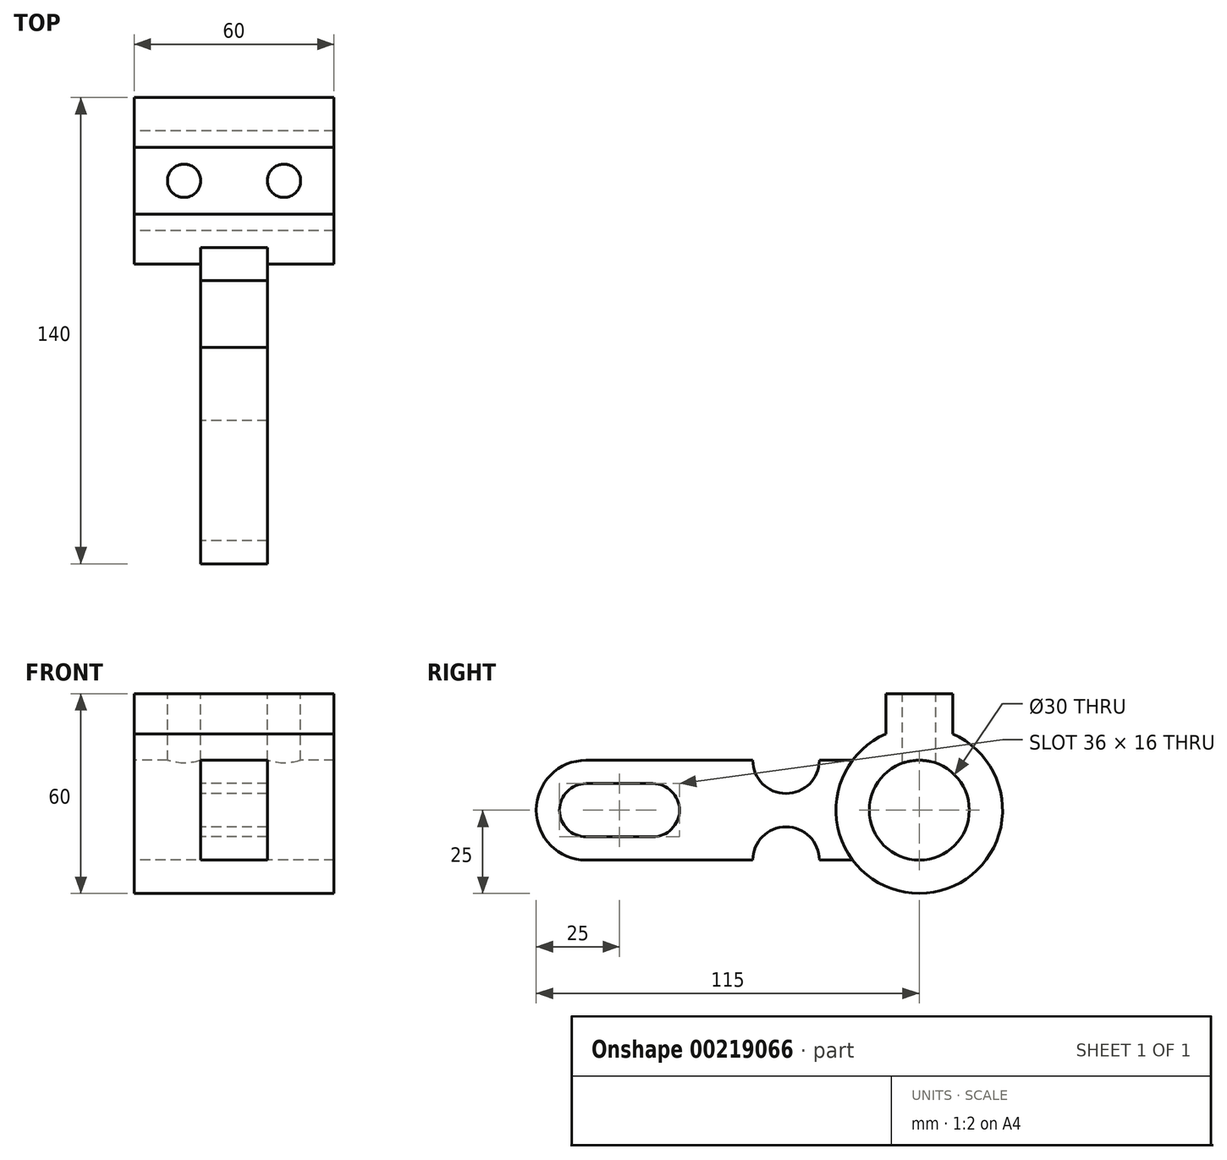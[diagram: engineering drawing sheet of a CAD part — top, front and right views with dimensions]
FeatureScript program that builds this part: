
annotation { "Feature Type Name" : "Feature", "Feature Type Description" : "" }
export const myFeature = defineFeature(function(context is Context, id is Id, definition is map)
    precondition{}
    {
        {
            var Q0;
            Q0=qCreatedBy(makeId("Right.planeOp"),FACE);
            var sketch = newSketch(context, id + "F0", { "sketchPlane" : qUnion([Q0])});
            skLineSegment(sketch, "E0", {"start": v(15, 0) * mm, "end": v(65, 0) * mm});
            skLineSegment(sketch, "E1", {"start": v(95, 30) * mm, "end": v(85, 30) * mm});
            skArc(sketch, "E2", {"start": v(15, 23) * mm, "mid": v(7, 15) * mm, "end": v(15, 7) * mm});
            skArc(sketch, "E3", {"start": v(65, 30) * mm, "mid": v(75, 20) * mm, "end": v(85, 30) * mm});
            skCircle(sketch, "E4", {"center": v(115, 15) * mm, "radius": 15 * mm});
            skArc(sketch, "E5", {"start": v(105, 37.91) * mm, "mid": v(115, -10) * mm, "end": v(125, 37.91) * mm});
            skArc(sketch, "E6", {"start": v(15, 30) * mm, "mid": v(0, 15) * mm, "end": v(15, 0) * mm});
            skLineSegment(sketch, "E7", {"start": v(115, 15) * mm, "end": v(-14.21, 15) * mm, "construction": true});
            skArc(sketch, "E8.MirrorC", {"start": v(65, 0) * mm, "mid": v(75, 10) * mm, "end": v(85, 0) * mm});
            skArc(sketch, "E9", {"start": v(35, 7) * mm, "mid": v(43, 15) * mm, "end": v(35, 23) * mm});
            skPoint(sketch, "E10.start.orphan", {"position": v(0, 30) * mm});
            skLineSegment(sketch, "E11", {"start": v(15, 23) * mm, "end": v(35, 23) * mm});
            skLineSegment(sketch, "E12", {"start": v(15, 7) * mm, "end": v(35, 7) * mm});
            skLineSegment(sketch, "E13.trimOffspring", {"start": v(85, 0) * mm, "end": v(95, 0) * mm});
            skLineSegment(sketch, "E14.trimOffspring", {"start": v(65, 30) * mm, "end": v(15, 30) * mm});
            skLineSegment(sketch, "E15.bottom", {"start": v(105, 50) * mm, "end": v(125, 50) * mm});
            skLineSegment(sketch, "E15.left", {"start": v(105, 50) * mm, "end": v(105, 37.91) * mm});
            skLineSegment(sketch, "E15.right", {"start": v(125, 50) * mm, "end": v(125, 37.91) * mm});
            skPoint(sketch, "E16.orphan", {"position": v(115, 30) * mm});
            skPoint(sketch, "E17.orphan", {"position": v(115, 0) * mm});
            skSolve(sketch);
        }
        {
            var Q0;
            Q0=makeQuery(id+"F0.imprint","IMPRINT",FACE,{"disambiguationData":[TD([[makeQuery(id+"F0.imprint","IMPRINT",EDGE,{"derivedFrom":sQuery(id+"F0.wireOp",EDGE,"E4")}),-1.0]])]});
            extrude(context, id + "F1", {"entities" : qUnion([Q0]), "endBound" : BoundingType.SYMMETRIC, "depth" : 60 * mm});
        }
        {
            var Q0;
            Q0=makeQuery(id+"F0.imprint","IMPRINT",FACE,{"disambiguationData":[TD([[makeQuery(id+"F0.imprint","IMPRINT",EDGE,{"derivedFrom":sQuery(id+"F0.wireOp",EDGE,"E0")}),1.0]])]});
            extrude(context, id + "F2", {"entities" : qUnion([Q0]), "operationType" : NewBodyOperationType.ADD, "endBound" : BoundingType.SYMMETRIC, "depth" : 20 * mm});
        }
        {
            var Q0;
            Q0=makeQuery(id+"F1.opExtrude","SWEPT_FACE",FACE,{"disambiguationData":[OSD([sQuery(id+"F0.wireOp",EDGE,"E15.bottom")])]});
            var sketch = newSketch(context, id + "F3", { "sketchPlane" : qUnion([Q0])});
            skCircle(sketch, "E18", {"center": v(15, 115) * mm, "radius": 5 * mm});
            skCircle(sketch, "E19.MirrorC", {"center": v(-15, 115) * mm, "radius": 5 * mm});
            skSolve(sketch);
        }
        {
            var Q0;
            Q0 = qSketchRegion(id + "F3", true);
            extrude(context, id + "F4", {"entities" : qUnion([Q0]), "operationType" : NewBodyOperationType.REMOVE, "endBound" : BoundingType.UP_TO_NEXT, "oppositeDirection" : true, "depth" : 25 * mm});
        }
    });
